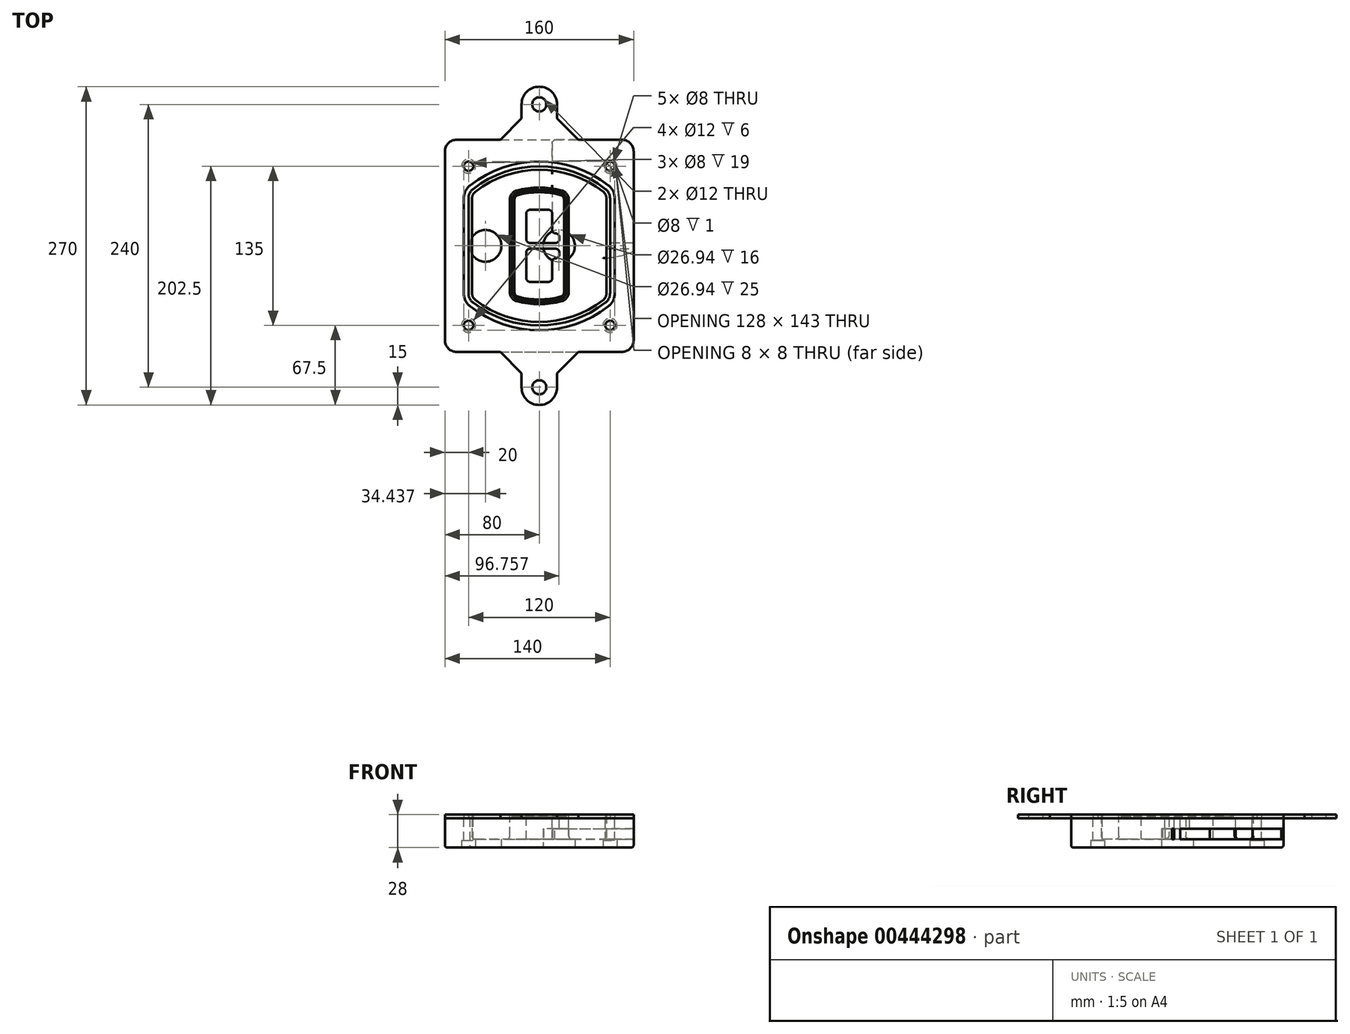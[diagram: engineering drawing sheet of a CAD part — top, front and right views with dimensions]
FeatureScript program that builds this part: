
annotation { "Feature Type Name" : "Feature", "Feature Type Description" : "" }
export const myFeature = defineFeature(function(context is Context, id is Id, definition is map)
    precondition{}
    {
        {
            var Q0;
            Q0=qCreatedBy(makeId("Top.planeOp"),FACE);
            var sketch = newSketch(context, id + "F0", { "sketchPlane" : qUnion([Q0])});
            skPoint(sketch, "E0.rect.middle", {"position": v(0, 0) * mm});
            skLineSegment(sketch, "E1.bottom", {"start": v(-70, -90) * mm, "end": v(70, -90) * mm});
            skLineSegment(sketch, "E1.top", {"start": v(-70, 90) * mm, "end": v(70, 90) * mm});
            skLineSegment(sketch, "E1.left", {"start": v(-80, -80) * mm, "end": v(-80, 80) * mm});
            skLineSegment(sketch, "E1.right", {"start": v(80, -80) * mm, "end": v(80, 80) * mm});
            skLineSegment(sketch, "E2", {"start": v(-80, 90) * mm, "end": v(80, -90) * mm, "construction": true});
            skLineSegment(sketch, "E3", {"start": v(80, 90) * mm, "end": v(-80, -90) * mm, "construction": true});
            skCircle(sketch, "E4", {"center": v(-60, 67.5) * mm, "radius": 4 * mm});
            skCircle(sketch, "E5", {"center": v(60, 67.5) * mm, "radius": 4 * mm});
            skCircle(sketch, "E6", {"center": v(60, -67.5) * mm, "radius": 4 * mm});
            skCircle(sketch, "E7", {"center": v(-60, -67.5) * mm, "radius": 4 * mm});
            skLineSegment(sketch, "E8", {"start": v(-60, 67.5) * mm, "end": v(60, 67.5) * mm, "construction": true});
            skLineSegment(sketch, "E9", {"start": v(60, 67.5) * mm, "end": v(60, -67.5) * mm, "construction": true});
            skLineSegment(sketch, "E10", {"start": v(60, -67.5) * mm, "end": v(-60, -67.5) * mm, "construction": true});
            skLineSegment(sketch, "E11", {"start": v(-60, -67.5) * mm, "end": v(-60, 67.5) * mm, "construction": true});
            skLineSegment(sketch, "E12", {"start": v(-60, 40.3) * mm, "end": v(-60, -40.3) * mm});
            skLineSegment(sketch, "E13", {"start": v(60, 40.3) * mm, "end": v(60, -40.3) * mm});
            skArc(sketch, "E14", {"start": v(56.15, 48.18) * mm, "mid": v(0, 67.5) * mm, "end": v(-56.15, 48.18) * mm});
            skArc(sketch, "E15", {"start": v(-56.15, -48.18) * mm, "mid": v(0, -67.5) * mm, "end": v(56.15, -48.18) * mm});
            skLineSegment(sketch, "E16", {"start": v(-60, 0) * mm, "end": v(60, 0) * mm, "construction": true});
            skPoint(sketch, "E17.visualSharp", {"position": v(-60, -45) * mm});
            skArc(sketch, "E17.filletArc", {"start": v(-60, -40.3) * mm, "mid": v(-58.99, -44.68) * mm, "end": v(-56.15, -48.18) * mm});
            skPoint(sketch, "E18.visualSharp", {"position": v(-60, 45) * mm});
            skArc(sketch, "E18.filletArc", {"start": v(-56.15, 48.18) * mm, "mid": v(-58.99, 44.68) * mm, "end": v(-60, 40.3) * mm});
            skPoint(sketch, "E19.visualSharp", {"position": v(60, 45) * mm});
            skArc(sketch, "E19.filletArc", {"start": v(60, 40.3) * mm, "mid": v(58.99, 44.68) * mm, "end": v(56.15, 48.18) * mm});
            skPoint(sketch, "E20.visualSharp", {"position": v(60, -45) * mm});
            skArc(sketch, "E20.filletArc", {"start": v(56.15, -48.18) * mm, "mid": v(58.99, -44.68) * mm, "end": v(60, -40.3) * mm});
            skPoint(sketch, "E21.visualSharp", {"position": v(-80, 90) * mm});
            skArc(sketch, "E21.filletArc", {"start": v(-70, 90) * mm, "mid": v(-77.07, 87.07) * mm, "end": v(-80, 80) * mm});
            skPoint(sketch, "E22.visualSharp", {"position": v(80, 90) * mm});
            skArc(sketch, "E22.filletArc", {"start": v(80, 80) * mm, "mid": v(77.07, 87.07) * mm, "end": v(70, 90) * mm});
            skPoint(sketch, "E23.visualSharp", {"position": v(80, -90) * mm});
            skArc(sketch, "E23.filletArc", {"start": v(70, -90) * mm, "mid": v(77.07, -87.07) * mm, "end": v(80, -80) * mm});
            skPoint(sketch, "E24.visualSharp", {"position": v(-80, -90) * mm});
            skArc(sketch, "E24.filletArc", {"start": v(-80, -80) * mm, "mid": v(-77.07, -87.07) * mm, "end": v(-70, -90) * mm});
            skArc(sketch, "E25.0", {"start": v(57, 40.3) * mm, "mid": v(56.3, 43.36) * mm, "end": v(54.3, 45.81) * mm});
            skLineSegment(sketch, "E25.1", {"start": v(57, 40.3) * mm, "end": v(57, -40.3) * mm});
            skArc(sketch, "E25.2", {"start": v(54.3, -45.81) * mm, "mid": v(56.3, -43.36) * mm, "end": v(57, -40.3) * mm});
            skArc(sketch, "E25.3", {"start": v(-54.3, -45.81) * mm, "mid": v(0, -64.5) * mm, "end": v(54.3, -45.81) * mm});
            skArc(sketch, "E25.4", {"start": v(-57, -40.3) * mm, "mid": v(-56.3, -43.36) * mm, "end": v(-54.3, -45.81) * mm});
            skArc(sketch, "E25.5", {"start": v(54.3, 45.81) * mm, "mid": v(0, 64.5) * mm, "end": v(-54.3, 45.81) * mm});
            skLineSegment(sketch, "E25.6", {"start": v(-57, 40.3) * mm, "end": v(-57, -40.3) * mm});
            skArc(sketch, "E25.7", {"start": v(-54.3, 45.81) * mm, "mid": v(-56.3, 43.36) * mm, "end": v(-57, 40.3) * mm});
            skArc(sketch, "E26.0", {"start": v(-58.62, 51.33) * mm, "mid": v(-62.58, 46.43) * mm, "end": v(-64, 40.3) * mm});
            skArc(sketch, "E26.1", {"start": v(58.62, 51.33) * mm, "mid": v(0, 71.5) * mm, "end": v(-58.62, 51.33) * mm});
            skArc(sketch, "E26.2", {"start": v(64, 40.3) * mm, "mid": v(62.58, 46.43) * mm, "end": v(58.62, 51.33) * mm});
            skLineSegment(sketch, "E26.3", {"start": v(64, 40.3) * mm, "end": v(64, -40.3) * mm});
            skArc(sketch, "E26.4", {"start": v(58.62, -51.33) * mm, "mid": v(62.58, -46.43) * mm, "end": v(64, -40.3) * mm});
            skLineSegment(sketch, "E26.5", {"start": v(-64, 40.3) * mm, "end": v(-64, -40.3) * mm});
            skArc(sketch, "E26.6", {"start": v(-58.62, -51.33) * mm, "mid": v(0, -71.5) * mm, "end": v(58.62, -51.33) * mm});
            skArc(sketch, "E26.7", {"start": v(-64, -40.3) * mm, "mid": v(-62.58, -46.43) * mm, "end": v(-58.62, -51.33) * mm});
            skCircle(sketch, "E27", {"center": v(0, 120) * mm, "radius": 6 * mm});
            skLineSegment(sketch, "E28", {"start": v(-15, 108) * mm, "end": v(-15, 120) * mm});
            skLineSegment(sketch, "E29", {"start": v(15, 108) * mm, "end": v(15, 120) * mm});
            skArc(sketch, "E30", {"start": v(15, 120) * mm, "mid": v(0, 135) * mm, "end": v(-15, 120) * mm});
            skLineSegment(sketch, "E31", {"start": v(-33, 90) * mm, "end": v(-15, 108) * mm});
            skLineSegment(sketch, "E32", {"start": v(15, 108) * mm, "end": v(33, 90) * mm});
            skLineSegment(sketch, "E33.MirrorCS", {"start": v(-33, -90) * mm, "end": v(-15, -108) * mm});
            skLineSegment(sketch, "E34.MirrorCS", {"start": v(-15, -108) * mm, "end": v(-15, -120) * mm});
            skCircle(sketch, "E35.MirrorC", {"center": v(0, -120) * mm, "radius": 6 * mm});
            skArc(sketch, "E36.MirrorCS", {"start": v(15, -120) * mm, "mid": v(0, -135) * mm, "end": v(-15, -120) * mm});
            skLineSegment(sketch, "E37.MirrorCS", {"start": v(15, -108) * mm, "end": v(15, -120) * mm});
            skLineSegment(sketch, "E38.MirrorCS", {"start": v(15, -108) * mm, "end": v(33, -90) * mm});
            skSolve(sketch);
        }
        {
            var Q0;
            Q0=makeQuery(id+"F0.imprint","IMPRINT",FACE,{"disambiguationData":[TD([[makeQuery(id+"F0.imprint","IMPRINT",EDGE,{"derivedFrom":sQuery(id+"F0.wireOp",EDGE,"E1.bottom")}),1.0]])]});
            var Q1;
            Q1=makeQuery(id+"F0.imprint","IMPRINT",FACE,{"disambiguationData":[TD([[makeQuery(id+"F0.imprint","IMPRINT",EDGE,{"derivedFrom":sQuery(id+"F0.wireOp",EDGE,"E12")}),1.0]])]});
            var Q2;
            Q2=makeQuery(id+"F0.imprint","IMPRINT",FACE,{"disambiguationData":[TD([[makeQuery(id+"F0.imprint","IMPRINT",EDGE,{"derivedFrom":sQuery(id+"F0.wireOp",EDGE,"E25.0")}),1.0]])]});
            var Q3;
            Q3=makeQuery(id+"F0.imprint","IMPRINT",FACE,{"disambiguationData":[TD([[makeQuery(id+"F0.imprint","IMPRINT",EDGE,{"derivedFrom":sQuery(id+"F0.wireOp",EDGE,"E12")}),-1.0]])]});
            extrude(context, id + "F1", {"entities" : qUnion([Q0, Q1, Q2, Q3]), "oppositeDirection" : true, "depth" : 25 * mm});
        }
        {
            var Q0;
            Q0=makeQuery(id+"F0.imprint","IMPRINT",FACE,{"disambiguationData":[TD([[makeQuery(id+"F0.imprint","IMPRINT",EDGE,{"derivedFrom":sQuery(id+"F0.wireOp",EDGE,"E12")}),1.0]])]});
            extrude(context, id + "F2", {"entities" : qUnion([Q0]), "operationType" : NewBodyOperationType.ADD, "depth" : 3 * mm});
        }
        {
            var Q0;
            Q0=makeQuery(id+"F0.imprint","IMPRINT",FACE,{"disambiguationData":[TD([[makeQuery(id+"F0.imprint","IMPRINT",EDGE,{"derivedFrom":sQuery(id+"F0.wireOp",EDGE,"E25.0")}),1.0]])]});
            extrude(context, id + "F3", {"entities" : qUnion([Q0]), "operationType" : NewBodyOperationType.REMOVE, "oppositeDirection" : true, "depth" : 18 * mm});
        }
        {
            var Q0;
            Q0=makeQuery(id+"F1.opExtrude","CAP_FACE",FACE,{"disambiguationData":[OSD([sQuery(id+"F0.wireOp",EDGE,"E1.bottom"),sQuery(id+"F0.wireOp",EDGE,"E1.top"),sQuery(id+"F0.wireOp",EDGE,"E1.left"),sQuery(id+"F0.wireOp",EDGE,"E1.right"),sQuery(id+"F0.wireOp",EDGE,"E4"),sQuery(id+"F0.wireOp",EDGE,"E5"),sQuery(id+"F0.wireOp",EDGE,"E6"),sQuery(id+"F0.wireOp",EDGE,"E7"),sQuery(id+"F0.wireOp",EDGE,"E21.filletArc"),sQuery(id+"F0.wireOp",EDGE,"E22.filletArc"),sQuery(id+"F0.wireOp",EDGE,"E23.filletArc"),sQuery(id+"F0.wireOp",EDGE,"E24.filletArc")])],"isStart":false});
            var sketch = newSketch(context, id + "F4", { "sketchPlane" : qUnion([Q0])});
            skCircle(sketch, "E39", {"center": v(16.76, 0) * mm, "radius": 13.47 * mm});
            skCircle(sketch, "E40", {"center": v(-45.56, 0) * mm, "radius": 13.47 * mm});
            skLineSegment(sketch, "E41", {"start": v(80, 0) * mm, "end": v(-80, 0) * mm});
            skCircle(sketch, "E42", {"center": v(16.76, 0) * mm, "radius": 18.47 * mm});
            skCircle(sketch, "E43", {"center": v(60, -67.5) * mm, "radius": 6 * mm});
            skCircle(sketch, "E44", {"center": v(-60, -67.5) * mm, "radius": 6 * mm});
            skCircle(sketch, "E45", {"center": v(-60, 67.5) * mm, "radius": 6 * mm});
            skCircle(sketch, "E46", {"center": v(60, 67.5) * mm, "radius": 6 * mm});
            skSolve(sketch);
        }
        {
            var Q0;
            Q0=makeQuery(id+"F2.opExtrude","CAP_FACE",FACE,{"disambiguationData":[OSD([sQuery(id+"F0.wireOp",EDGE,"E12"),sQuery(id+"F0.wireOp",EDGE,"E13"),sQuery(id+"F0.wireOp",EDGE,"E14"),sQuery(id+"F0.wireOp",EDGE,"E15"),sQuery(id+"F0.wireOp",EDGE,"E17.filletArc"),sQuery(id+"F0.wireOp",EDGE,"E18.filletArc"),sQuery(id+"F0.wireOp",EDGE,"E19.filletArc"),sQuery(id+"F0.wireOp",EDGE,"E20.filletArc"),sQuery(id+"F0.wireOp",EDGE,"E25.0"),sQuery(id+"F0.wireOp",EDGE,"E25.1"),sQuery(id+"F0.wireOp",EDGE,"E25.2"),sQuery(id+"F0.wireOp",EDGE,"E25.3"),sQuery(id+"F0.wireOp",EDGE,"E25.4"),sQuery(id+"F0.wireOp",EDGE,"E25.5"),sQuery(id+"F0.wireOp",EDGE,"E25.6"),sQuery(id+"F0.wireOp",EDGE,"E25.7")])],"isStart":false});
            var sketch = newSketch(context, id + "F5", { "sketchPlane" : qUnion([Q0])});
            skArc(sketch, "E47.0", {"start": v(-19.08, -46.97) * mm, "mid": v(0, -49.5) * mm, "end": v(19.08, -46.97) * mm});
            skArc(sketch, "E48.0", {"start": v(19.08, 46.97) * mm, "mid": v(0, 49.5) * mm, "end": v(-19.08, 46.97) * mm});
            skLineSegment(sketch, "E49", {"start": v(-25, 39.25) * mm, "end": v(-25, -39.25) * mm});
            skLineSegment(sketch, "E50", {"start": v(25, 39.25) * mm, "end": v(25, -39.25) * mm});
            skLineSegment(sketch, "E51", {"start": v(-25, 45.1) * mm, "end": v(25, 45.1) * mm, "construction": true});
            skLineSegment(sketch, "E52", {"start": v(-25, -45.1) * mm, "end": v(25, -45.1) * mm, "construction": true});
            skPoint(sketch, "E53.visualSharp", {"position": v(-25, 45.1) * mm});
            skArc(sketch, "E53.filletArc", {"start": v(-19.08, 46.97) * mm, "mid": v(-23.35, 44.11) * mm, "end": v(-25, 39.25) * mm});
            skPoint(sketch, "E54.visualSharp", {"position": v(25, 45.1) * mm});
            skArc(sketch, "E54.filletArc", {"start": v(25, 39.25) * mm, "mid": v(23.35, 44.11) * mm, "end": v(19.08, 46.97) * mm});
            skPoint(sketch, "E55.visualSharp", {"position": v(25, -45.1) * mm});
            skArc(sketch, "E55.filletArc", {"start": v(19.08, -46.97) * mm, "mid": v(23.35, -44.11) * mm, "end": v(25, -39.25) * mm});
            skPoint(sketch, "E56.visualSharp", {"position": v(-25, -45.1) * mm});
            skArc(sketch, "E56.filletArc", {"start": v(-25, -39.25) * mm, "mid": v(-23.35, -44.11) * mm, "end": v(-19.08, -46.97) * mm});
            skArc(sketch, "E57.0", {"start": v(54.3, 45.81) * mm, "mid": v(0, 64.5) * mm, "end": v(-54.3, 45.81) * mm});
            skArc(sketch, "E57.1", {"start": v(-54.3, 45.81) * mm, "mid": v(-56.3, 43.36) * mm, "end": v(-57, 40.3) * mm});
            skLineSegment(sketch, "E57.2", {"start": v(-57, 40.3) * mm, "end": v(-57, -40.3) * mm});
            skArc(sketch, "E57.3", {"start": v(-57, -40.3) * mm, "mid": v(-56.3, -43.36) * mm, "end": v(-54.3, -45.81) * mm});
            skArc(sketch, "E57.4", {"start": v(-54.3, -45.81) * mm, "mid": v(0, -64.5) * mm, "end": v(54.3, -45.81) * mm});
            skArc(sketch, "E57.5", {"start": v(54.3, -45.81) * mm, "mid": v(56.3, -43.36) * mm, "end": v(57, -40.3) * mm});
            skLineSegment(sketch, "E57.6", {"start": v(57, 40.3) * mm, "end": v(57, -40.3) * mm});
            skArc(sketch, "E57.7", {"start": v(57, 40.3) * mm, "mid": v(56.3, 43.36) * mm, "end": v(54.3, 45.81) * mm});
            skLineSegment(sketch, "E58.0", {"start": v(23, 39.25) * mm, "end": v(23, -39.25) * mm});
            skArc(sketch, "E58.1", {"start": v(18.56, -45.04) * mm, "mid": v(21.76, -42.9) * mm, "end": v(23, -39.25) * mm});
            skArc(sketch, "E58.2", {"start": v(-18.56, -45.04) * mm, "mid": v(0, -47.5) * mm, "end": v(18.56, -45.04) * mm});
            skArc(sketch, "E58.3", {"start": v(-23, -39.25) * mm, "mid": v(-21.76, -42.9) * mm, "end": v(-18.56, -45.04) * mm});
            skLineSegment(sketch, "E58.4", {"start": v(-23, 39.25) * mm, "end": v(-23, -39.25) * mm});
            skArc(sketch, "E58.5", {"start": v(23, 39.25) * mm, "mid": v(21.76, 42.9) * mm, "end": v(18.56, 45.04) * mm});
            skArc(sketch, "E58.6", {"start": v(-18.56, 45.04) * mm, "mid": v(-21.76, 42.9) * mm, "end": v(-23, 39.25) * mm});
            skArc(sketch, "E58.7", {"start": v(18.56, 45.04) * mm, "mid": v(0, 47.5) * mm, "end": v(-18.56, 45.04) * mm});
            skArc(sketch, "E59.0", {"start": v(21, 39.25) * mm, "mid": v(20.18, 41.68) * mm, "end": v(18.04, 43.1) * mm});
            skLineSegment(sketch, "E59.1", {"start": v(21, 39.25) * mm, "end": v(21, -39.25) * mm});
            skArc(sketch, "E59.2", {"start": v(18.04, -43.1) * mm, "mid": v(20.18, -41.68) * mm, "end": v(21, -39.25) * mm});
            skArc(sketch, "E59.3", {"start": v(-18.04, -43.1) * mm, "mid": v(0, -45.5) * mm, "end": v(18.04, -43.1) * mm});
            skArc(sketch, "E59.4", {"start": v(-21, -39.25) * mm, "mid": v(-20.18, -41.68) * mm, "end": v(-18.04, -43.1) * mm});
            skArc(sketch, "E59.5", {"start": v(18.04, 43.1) * mm, "mid": v(0, 45.5) * mm, "end": v(-18.04, 43.1) * mm});
            skLineSegment(sketch, "E59.6", {"start": v(-21, 39.25) * mm, "end": v(-21, -39.25) * mm});
            skArc(sketch, "E59.7", {"start": v(-18.04, 43.1) * mm, "mid": v(-20.18, 41.68) * mm, "end": v(-21, 39.25) * mm});
            skLineSegment(sketch, "E60", {"start": v(-25, 0) * mm, "end": v(25, 0) * mm, "construction": true});
            skLineSegment(sketch, "E61", {"start": v(-11, 5.5) * mm, "end": v(-11, 27.5) * mm});
            skLineSegment(sketch, "E62", {"start": v(-8, 30.5) * mm, "end": v(8, 30.5) * mm});
            skLineSegment(sketch, "E63", {"start": v(11, 27.5) * mm, "end": v(11, 13.5) * mm});
            skLineSegment(sketch, "E64", {"start": v(14, 10.5) * mm, "end": v(14, 10.5) * mm});
            skLineSegment(sketch, "E65", {"start": v(17, 7.5) * mm, "end": v(17, 5.5) * mm});
            skLineSegment(sketch, "E66", {"start": v(14, 2.5) * mm, "end": v(-8, 2.5) * mm});
            skPoint(sketch, "E67.visualSharp", {"position": v(-11, 30.5) * mm});
            skArc(sketch, "E67.filletArc", {"start": v(-8, 30.5) * mm, "mid": v(-10.12, 29.62) * mm, "end": v(-11, 27.5) * mm});
            skPoint(sketch, "E68.visualSharp", {"position": v(11, 30.5) * mm});
            skArc(sketch, "E68.filletArc", {"start": v(11, 27.5) * mm, "mid": v(10.12, 29.62) * mm, "end": v(8, 30.5) * mm});
            skPoint(sketch, "E69.visualSharp", {"position": v(11, 10.5) * mm});
            skArc(sketch, "E69.filletArc", {"start": v(11, 13.5) * mm, "mid": v(11.88, 11.38) * mm, "end": v(14, 10.5) * mm});
            skPoint(sketch, "E70.visualSharp", {"position": v(17, 10.5) * mm});
            skArc(sketch, "E70.filletArc", {"start": v(17, 7.5) * mm, "mid": v(16.12, 9.62) * mm, "end": v(14, 10.5) * mm});
            skPoint(sketch, "E71.visualSharp", {"position": v(17, 2.5) * mm});
            skArc(sketch, "E71.filletArc", {"start": v(14, 2.5) * mm, "mid": v(16.12, 3.38) * mm, "end": v(17, 5.5) * mm});
            skPoint(sketch, "E72.visualSharp", {"position": v(-11, 2.5) * mm});
            skArc(sketch, "E72.filletArc", {"start": v(-11, 5.5) * mm, "mid": v(-10.12, 3.38) * mm, "end": v(-8, 2.5) * mm});
            skLineSegment(sketch, "E73.0.MirrorCS", {"start": v(14, -2.5) * mm, "end": v(-8, -2.5) * mm});
            skArc(sketch, "E74.0.MirrorCS", {"start": v(-11, -5.5) * mm, "mid": v(-10.12, -3.38) * mm, "end": v(-8, -2.5) * mm});
            skLineSegment(sketch, "E75.0.MirrorCS", {"start": v(-11, -5.5) * mm, "end": v(-11, -27.5) * mm});
            skArc(sketch, "E76.0.MirrorCS", {"start": v(-8, -30.5) * mm, "mid": v(-10.12, -29.62) * mm, "end": v(-11, -27.5) * mm});
            skLineSegment(sketch, "E77.0.MirrorCS", {"start": v(-8, -30.5) * mm, "end": v(8, -30.5) * mm});
            skArc(sketch, "E78.0.MirrorCS", {"start": v(11, -27.5) * mm, "mid": v(10.12, -29.62) * mm, "end": v(8, -30.5) * mm});
            skLineSegment(sketch, "E79.0.MirrorCS", {"start": v(11, -27.5) * mm, "end": v(11, -13.5) * mm});
            skArc(sketch, "E80.0.MirrorCS", {"start": v(11, -13.5) * mm, "mid": v(11.88, -11.38) * mm, "end": v(14, -10.5) * mm});
            skArc(sketch, "E81.0.MirrorCS", {"start": v(17, -7.5) * mm, "mid": v(16.12, -9.62) * mm, "end": v(14, -10.5) * mm});
            skLineSegment(sketch, "E82.0.MirrorCS", {"start": v(17, -7.5) * mm, "end": v(17, -5.5) * mm});
            skArc(sketch, "E83.0.MirrorCS", {"start": v(14, -2.5) * mm, "mid": v(16.12, -3.38) * mm, "end": v(17, -5.5) * mm});
            skSolve(sketch);
        }
        {
            var Q0;
            Q0=makeQuery(id+"F5.imprint","IMPRINT",FACE,{"disambiguationData":[TD([[makeQuery(id+"F5.imprint","IMPRINT",EDGE,{"derivedFrom":sQuery(id+"F5.wireOp",EDGE,"E47.0")}),1.0]])]});
            var Q1;
            Q1=makeQuery(id+"F5.imprint","IMPRINT",FACE,{"disambiguationData":[TD([[makeQuery(id+"F5.imprint","IMPRINT",EDGE,{"derivedFrom":sQuery(id+"F5.wireOp",EDGE,"E58.0")}),-1.0]])]});
            var Q2;
            Q2=makeQuery(id+"F5.imprint","IMPRINT",FACE,{"disambiguationData":[TD([[makeQuery(id+"F5.imprint","IMPRINT",EDGE,{"derivedFrom":sQuery(id+"F5.wireOp",EDGE,"E59.0")}),1.0]])]});
            extrude(context, id + "F6", {"entities" : qUnion([Q0, Q1, Q2]), "operationType" : NewBodyOperationType.ADD, "endBound" : BoundingType.UP_TO_NEXT, "oppositeDirection" : true, "depth" : 25 * mm});
        }
        {
            var Q0;
            Q0=makeQuery(id+"F5.imprint","IMPRINT",FACE,{"disambiguationData":[TD([[makeQuery(id+"F5.imprint","IMPRINT",EDGE,{"derivedFrom":sQuery(id+"F5.wireOp",EDGE,"E58.0")}),-1.0]])]});
            extrude(context, id + "F7", {"entities" : qUnion([Q0]), "operationType" : NewBodyOperationType.REMOVE, "oppositeDirection" : true, "depth" : 2 * mm});
        }
        {
            var Q0;
            {var subQ0=sQuery(id+"F4.wireOp",EDGE,"E41");var subQ1=sQuery(id+"F4.wireOp",EDGE,"E39");var subQ3=makeQuery(id+"F4.imprint","INTERSECT",VERTEX,{"disambiguationData":[OD(0.0)],"derivedFrom":[subQ1,subQ0]});Q0=makeQuery(id+"F4.imprint","IMPRINT",FACE,{"disambiguationData":[TD([[makeQuery(id+"F4.imprint","IMPRINT",EDGE,{"disambiguationData":[TD([[subQ3,-1.0]])],"derivedFrom":subQ1}),1.0]])]});}
            var Q1;
            {var subQ0=sQuery(id+"F4.wireOp",EDGE,"E41");var subQ1=sQuery(id+"F4.wireOp",EDGE,"E39");var subQ3=makeQuery(id+"F4.imprint","INTERSECT",VERTEX,{"disambiguationData":[OD(0.0)],"derivedFrom":[subQ1,subQ0]});Q1=makeQuery(id+"F4.imprint","IMPRINT",FACE,{"disambiguationData":[TD([[makeQuery(id+"F4.imprint","IMPRINT",EDGE,{"disambiguationData":[TD([[subQ3,1.0]])],"derivedFrom":subQ1}),1.0]])]});}
            extrude(context, id + "F8", {"entities" : qUnion([Q0, Q1]), "operationType" : NewBodyOperationType.REMOVE, "oppositeDirection" : true, "depth" : 16 * mm});
        }
        {
            var Q0;
            {var subQ0=sQuery(id+"F4.wireOp",EDGE,"E41");var subQ1=sQuery(id+"F4.wireOp",EDGE,"E40");var subQ3=makeQuery(id+"F4.imprint","INTERSECT",VERTEX,{"disambiguationData":[OD(0.0)],"derivedFrom":[subQ1,subQ0]});Q0=makeQuery(id+"F4.imprint","IMPRINT",FACE,{"disambiguationData":[TD([[makeQuery(id+"F4.imprint","IMPRINT",EDGE,{"disambiguationData":[TD([[subQ3,-1.0]])],"derivedFrom":subQ1}),1.0]])]});}
            var Q1;
            {var subQ0=sQuery(id+"F4.wireOp",EDGE,"E41");var subQ1=sQuery(id+"F4.wireOp",EDGE,"E40");var subQ3=makeQuery(id+"F4.imprint","INTERSECT",VERTEX,{"disambiguationData":[OD(0.0)],"derivedFrom":[subQ1,subQ0]});Q1=makeQuery(id+"F4.imprint","IMPRINT",FACE,{"disambiguationData":[TD([[makeQuery(id+"F4.imprint","IMPRINT",EDGE,{"disambiguationData":[TD([[subQ3,1.0]])],"derivedFrom":subQ1}),1.0]])]});}
            extrude(context, id + "F9", {"entities" : qUnion([Q0, Q1]), "operationType" : NewBodyOperationType.REMOVE, "oppositeDirection" : true, "depth" : 25 * mm});
        }
        {
            var Q0;
            Q0=makeQuery(id+"F4.imprint","IMPRINT",FACE,{"disambiguationData":[TD([[makeQuery(id+"F4.imprint","IMPRINT",EDGE,{"derivedFrom":sQuery(id+"F4.wireOp",EDGE,"E43")}),1.0]])]});
            var Q1;
            Q1=makeQuery(id+"F4.imprint","IMPRINT",FACE,{"disambiguationData":[TD([[makeQuery(id+"F4.imprint","IMPRINT",EDGE,{"derivedFrom":makeQuery(id+"F1.opExtrude","CAP_EDGE",EDGE,{"disambiguationData":[OSD([sQuery(id+"F0.wireOp",EDGE,"E5")])],"isStart":false})}),-1.0]])]});
            var Q2;
            Q2=makeQuery(id+"F4.imprint","IMPRINT",FACE,{"disambiguationData":[TD([[makeQuery(id+"F4.imprint","IMPRINT",EDGE,{"derivedFrom":sQuery(id+"F4.wireOp",EDGE,"E44")}),1.0]])]});
            var Q3;
            Q3=makeQuery(id+"F4.imprint","IMPRINT",FACE,{"disambiguationData":[TD([[makeQuery(id+"F4.imprint","IMPRINT",EDGE,{"derivedFrom":makeQuery(id+"F1.opExtrude","CAP_EDGE",EDGE,{"disambiguationData":[OSD([sQuery(id+"F0.wireOp",EDGE,"E4")])],"isStart":false})}),-1.0]])]});
            var Q4;
            Q4=makeQuery(id+"F4.imprint","IMPRINT",FACE,{"disambiguationData":[TD([[makeQuery(id+"F4.imprint","IMPRINT",EDGE,{"derivedFrom":sQuery(id+"F4.wireOp",EDGE,"E45")}),1.0]])]});
            var Q5;
            Q5=makeQuery(id+"F4.imprint","IMPRINT",FACE,{"disambiguationData":[TD([[makeQuery(id+"F4.imprint","IMPRINT",EDGE,{"derivedFrom":makeQuery(id+"F1.opExtrude","CAP_EDGE",EDGE,{"disambiguationData":[OSD([sQuery(id+"F0.wireOp",EDGE,"E7")])],"isStart":false})}),-1.0]])]});
            var Q6;
            Q6=makeQuery(id+"F4.imprint","IMPRINT",FACE,{"disambiguationData":[TD([[makeQuery(id+"F4.imprint","IMPRINT",EDGE,{"derivedFrom":sQuery(id+"F4.wireOp",EDGE,"E46")}),1.0]])]});
            var Q7;
            Q7=makeQuery(id+"F4.imprint","IMPRINT",FACE,{"disambiguationData":[TD([[makeQuery(id+"F4.imprint","IMPRINT",EDGE,{"derivedFrom":makeQuery(id+"F1.opExtrude","CAP_EDGE",EDGE,{"disambiguationData":[OSD([sQuery(id+"F0.wireOp",EDGE,"E6")])],"isStart":false})}),-1.0]])]});
            extrude(context, id + "F10", {"entities" : qUnion([Q0, Q1, Q2, Q3, Q4, Q5, Q6, Q7]), "operationType" : NewBodyOperationType.REMOVE, "oppositeDirection" : true, "depth" : 6 * mm});
        }
        {
            var Q0;
            Q0=makeQuery(id+"F8.boolean.opBoolean","COPY",FACE,{"derivedFrom":makeQuery(id+"F8.opExtrude","CAP_FACE",FACE,{"disambiguationData":[OSD([sQuery(id+"F4.wireOp",EDGE,"E39")])],"isStart":false})});
            var sketch = newSketch(context, id + "F11", { "sketchPlane" : qUnion([Q0])});
            skArc(sketch, "E84.0", {"start": v(11, -88.19) * mm, "mid": v(97.1, -83.6) * mm, "end": v(92.5, 2.5) * mm});
            skArc(sketch, "E84.1", {"start": v(92.5, -2.5) * mm, "mid": v(-5.53, -19.03) * mm, "end": v(11, -117.08) * mm});
            skLineSegment(sketch, "E85", {"start": v(14, -2.5) * mm, "end": v(92.5, -2.5) * mm});
            skLineSegment(sketch, "E86.0", {"start": v(92.5, 2.5) * mm, "end": v(14, 2.5) * mm});
            skArc(sketch, "E86.1", {"start": v(14, 2.5) * mm, "mid": v(16.12, 3.38) * mm, "end": v(17, 5.5) * mm});
            skLineSegment(sketch, "E86.2", {"start": v(17, 7.5) * mm, "end": v(17, 5.5) * mm});
            skArc(sketch, "E86.3", {"start": v(17, 7.5) * mm, "mid": v(16.12, 9.62) * mm, "end": v(14, 10.5) * mm});
            skArc(sketch, "E86.4", {"start": v(11, 13.5) * mm, "mid": v(11.88, 11.38) * mm, "end": v(14, 10.5) * mm});
            skLineSegment(sketch, "E86.5", {"start": v(11, 13.5) * mm, "end": v(11, -88.19) * mm});
            skLineSegment(sketch, "E86.7", {"start": v(92.5, -2.5) * mm, "end": v(14, -2.5) * mm});
            skArc(sketch, "E86.8", {"start": v(14, -2.5) * mm, "mid": v(16.12, -3.38) * mm, "end": v(17, -5.5) * mm});
            skLineSegment(sketch, "E86.9", {"start": v(17, -7.5) * mm, "end": v(17, -5.5) * mm});
            skArc(sketch, "E86.10", {"start": v(17, -7.5) * mm, "mid": v(16.12, -9.62) * mm, "end": v(14, -10.5) * mm});
            skArc(sketch, "E86.11", {"start": v(11, -13.5) * mm, "mid": v(11.88, -11.38) * mm, "end": v(14, -10.5) * mm});
            skLineSegment(sketch, "E86.12", {"start": v(11, -117.08) * mm, "end": v(11, -13.5) * mm});
            skPoint(sketch, "E87.orphan", {"position": v(11, -27.5) * mm});
            skPoint(sketch, "E88.orphan", {"position": v(-8, -2.5) * mm});
            skPoint(sketch, "E89.orphan", {"position": v(-8, 2.5) * mm});
            skPoint(sketch, "E90.orphan", {"position": v(11, 27.5) * mm});
            skSolve(sketch);
        }
        {
            var Q0;
            {var subQ7=sQuery(id+"F11.wireOp",EDGE,"E84.0");var subQ14=sQuery(id+"F11.wireOp",EDGE,"E84.1");var subQ16=sQuery(id+"F11.wireOp",EDGE,"E86.1");var subQ18=sQuery(id+"F11.wireOp",EDGE,"E86.8");Q0=qUnion([makeQuery(id+"F11.imprint","IMPRINT",FACE,{"disambiguationData":[TD([[makeQuery(id+"F11.imprint","IMPRINT",EDGE,{"derivedFrom":subQ7}),1.0]])]}),makeQuery(id+"F11.imprint","IMPRINT",FACE,{"disambiguationData":[TD([[makeQuery(id+"F11.imprint","IMPRINT",EDGE,{"derivedFrom":subQ14}),1.0]])]}),makeQuery(id+"F11.imprint","IMPRINT",FACE,{"disambiguationData":[TD([[makeQuery(id+"F11.imprint","IMPRINT",EDGE,{"derivedFrom":subQ16}),1.0]])]}),makeQuery(id+"F11.imprint","IMPRINT",FACE,{"disambiguationData":[TD([[makeQuery(id+"F11.imprint","IMPRINT",EDGE,{"derivedFrom":subQ18}),-1.0]])]})]);}
            var Q1;
            Q1=makeQuery(id+"F6.boolean.opBoolean","SPLIT",FACE,{"disambiguationData":[TD([makeQuery(id+"F6.opExtrude","SWEPT_FACE",FACE,{"disambiguationData":[OSD([sQuery(id+"F5.wireOp",EDGE,"E61")])]})])],"derivedFrom":makeQuery(id+"F3.boolean.opBoolean","COPY",FACE,{"derivedFrom":makeQuery(id+"F3.opExtrude","CAP_FACE",FACE,{"disambiguationData":[OSD([sQuery(id+"F0.wireOp",EDGE,"E25.0"),sQuery(id+"F0.wireOp",EDGE,"E25.1"),sQuery(id+"F0.wireOp",EDGE,"E25.2"),sQuery(id+"F0.wireOp",EDGE,"E25.3"),sQuery(id+"F0.wireOp",EDGE,"E25.4"),sQuery(id+"F0.wireOp",EDGE,"E25.5"),sQuery(id+"F0.wireOp",EDGE,"E25.6"),sQuery(id+"F0.wireOp",EDGE,"E25.7")])],"isStart":false})})});
            extrude(context, id + "F12", {"entities" : qUnion([Q0]), "operationType" : NewBodyOperationType.REMOVE, "endBound" : BoundingType.UP_TO_SURFACE, "endBoundEntityFace" : qUnion([Q1]), "depth" : 25 * mm});
        }
        {
            var Q0;
            Q0=makeQuery(id+"F3.boolean.opBoolean","COPY",EDGE,{"derivedFrom":makeQuery(id+"F3.opExtrude","CAP_EDGE",EDGE,{"disambiguationData":[OSD([sQuery(id+"F0.wireOp",EDGE,"E25.6")])],"isStart":false})});
            var Q1;
            Q1=makeQuery(id+"FcX3RilgP8JfTuH_1.boolean.opBoolean","INTERSECT",EDGE,{"derivedFrom":[makeQuery(id+"F6.opExtrude","SWEPT_FACE",FACE,{"disambiguationData":[OSD([sQuery(id+"F5.wireOp",EDGE,"E50")])]}),makeQuery(id+"FcX3RilgP8JfTuH_1.opExtrude","CAP_FACE",FACE,{"disambiguationData":[OSD([sQuery(id+"F4.wireOp",EDGE,"E42")])],"isStart":false})]});
            var Q2;
            Q2=makeQuery(id+"FcX3RilgP8JfTuH_1.boolean.opBoolean","INTERSECT",EDGE,{"disambiguationData":[OD(1.0)],"derivedFrom":[makeQuery(id+"F6.opExtrude","SWEPT_FACE",FACE,{"disambiguationData":[OSD([sQuery(id+"F5.wireOp",EDGE,"E50")])]}),makeQuery(id+"FcX3RilgP8JfTuH_1.opExtrude","SWEPT_FACE",FACE,{"disambiguationData":[OSD([sQuery(id+"F4.wireOp",EDGE,"E42")])]})]});
            var Q3;
            {var subQ0=sQuery(id+"F5.wireOp",EDGE,"E50");Q3=makeQuery(id+"F8.boolean.opBoolean","SPLIT",EDGE,{"disambiguationData":[TD([makeQuery(id+"F6.opExtrude","SWEPT_FACE",FACE,{"disambiguationData":[OSD([sQuery(id+"F5.wireOp",EDGE,"E55.filletArc")])]})])],"derivedFrom":makeQuery(id+"F6.opExtrude","CAP_EDGE",EDGE,{"disambiguationData":[OSD([subQ0])],"isStart":false})});}
            var Q4;
            {var subQ0=sQuery(id+"F0.wireOp",EDGE,"E25.0");var subQ1=sQuery(id+"F0.wireOp",EDGE,"E25.1");var subQ2=sQuery(id+"F0.wireOp",EDGE,"E25.2");var subQ3=sQuery(id+"F0.wireOp",EDGE,"E25.3");var subQ4=sQuery(id+"F0.wireOp",EDGE,"E25.4");var subQ5=sQuery(id+"F0.wireOp",EDGE,"E25.5");var subQ6=sQuery(id+"F0.wireOp",EDGE,"E25.6");var subQ7=sQuery(id+"F0.wireOp",EDGE,"E25.7");Q4=makeQuery(id+"FcX3RilgP8JfTuH_1.boolean.opBoolean","INTERSECT",EDGE,{"derivedFrom":[makeQuery(id+"F6.boolean.opBoolean","SPLIT",FACE,{"disambiguationData":[TD([makeQuery(id+"F2.opExtrude","SWEPT_FACE",FACE,{"disambiguationData":[OSD([subQ0])]})])],"derivedFrom":makeQuery(id+"F3.boolean.opBoolean","COPY",FACE,{"derivedFrom":makeQuery(id+"F3.opExtrude","CAP_FACE",FACE,{"disambiguationData":[OSD([subQ0,subQ1,subQ2,subQ3,subQ4,subQ5,subQ6,subQ7])],"isStart":false})})}),makeQuery(id+"FcX3RilgP8JfTuH_1.opExtrude","SWEPT_FACE",FACE,{"disambiguationData":[OSD([sQuery(id+"F4.wireOp",EDGE,"E42")])]})]});}
            var Q5;
            Q5=makeQuery(id+"FcX3RilgP8JfTuH_1.boolean.opBoolean","INTERSECT",EDGE,{"disambiguationData":[OD(0.0)],"derivedFrom":[makeQuery(id+"F6.opExtrude","SWEPT_FACE",FACE,{"disambiguationData":[OSD([sQuery(id+"F5.wireOp",EDGE,"E50")])]}),makeQuery(id+"FcX3RilgP8JfTuH_1.opExtrude","SWEPT_FACE",FACE,{"disambiguationData":[OSD([sQuery(id+"F4.wireOp",EDGE,"E42")])]})]});
            fillet(context, id + "F13", {"entities" : qUnion([Q0, Q1, Q2, Q3, Q4, Q5]), "radius" : 3 * mm, "tangentPropagation" : true, "allowEdgeOverflow" : false});
        }
        {
            var Q0;
            Q0=makeQuery(id+"F1.opExtrude","CAP_EDGE",EDGE,{"disambiguationData":[OSD([sQuery(id+"F0.wireOp",EDGE,"E1.bottom")])],"isStart":false});
            fillet(context, id + "F14", {"entities" : qUnion([Q0]), "radius" : 2 * mm, "tangentPropagation" : true, "allowEdgeOverflow" : false});
        }
        {
            var Q0;
            Q0 = qSketchRegion(id + "F0", true);
            var Q1;
            Q1=makeQuery(id+"F2.opExtrude","CAP_FACE",FACE,{"disambiguationData":[OSD([sQuery(id+"F0.wireOp",EDGE,"E12"),sQuery(id+"F0.wireOp",EDGE,"E13"),sQuery(id+"F0.wireOp",EDGE,"E14"),sQuery(id+"F0.wireOp",EDGE,"E15"),sQuery(id+"F0.wireOp",EDGE,"E17.filletArc"),sQuery(id+"F0.wireOp",EDGE,"E18.filletArc"),sQuery(id+"F0.wireOp",EDGE,"E19.filletArc"),sQuery(id+"F0.wireOp",EDGE,"E20.filletArc"),sQuery(id+"F0.wireOp",EDGE,"E25.0"),sQuery(id+"F0.wireOp",EDGE,"E25.1"),sQuery(id+"F0.wireOp",EDGE,"E25.2"),sQuery(id+"F0.wireOp",EDGE,"E25.3"),sQuery(id+"F0.wireOp",EDGE,"E25.4"),sQuery(id+"F0.wireOp",EDGE,"E25.5"),sQuery(id+"F0.wireOp",EDGE,"E25.6"),sQuery(id+"F0.wireOp",EDGE,"E25.7")])],"isStart":false});
            extrude(context, id + "F15", {"entities" : qUnion([Q0]), "endBound" : BoundingType.UP_TO_SURFACE, "endBoundEntityFace" : qUnion([Q1]), "depth" : 3.5 * mm});
        }
        {
            var Q0;
            Q0=makeQuery(id+"F15.opExtrude","SWEPT_BODY",BODY,{"disambiguationData":[OSD([sQuery(id+"F0.wireOp",EDGE,"E1.bottom"),sQuery(id+"F0.wireOp",EDGE,"E1.top"),sQuery(id+"F0.wireOp",EDGE,"E1.left"),sQuery(id+"F0.wireOp",EDGE,"E1.right"),sQuery(id+"F0.wireOp",EDGE,"E4"),sQuery(id+"F0.wireOp",EDGE,"E5"),sQuery(id+"F0.wireOp",EDGE,"E6"),sQuery(id+"F0.wireOp",EDGE,"E7"),sQuery(id+"F0.wireOp",EDGE,"E21.filletArc"),sQuery(id+"F0.wireOp",EDGE,"E22.filletArc"),sQuery(id+"F0.wireOp",EDGE,"E23.filletArc"),sQuery(id+"F0.wireOp",EDGE,"E24.filletArc"),sQuery(id+"F0.wireOp",EDGE,"E26.0"),sQuery(id+"F0.wireOp",EDGE,"E26.1"),sQuery(id+"F0.wireOp",EDGE,"E26.2"),sQuery(id+"F0.wireOp",EDGE,"E26.3"),sQuery(id+"F0.wireOp",EDGE,"E26.4"),sQuery(id+"F0.wireOp",EDGE,"E26.5"),sQuery(id+"F0.wireOp",EDGE,"E26.6"),sQuery(id+"F0.wireOp",EDGE,"E26.7"),sQuery(id+"F0.wireOp",EDGE,"E27"),sQuery(id+"F0.wireOp",EDGE,"E28"),sQuery(id+"F0.wireOp",EDGE,"E29"),sQuery(id+"F0.wireOp",EDGE,"E30"),sQuery(id+"F0.wireOp",EDGE,"E31"),sQuery(id+"F0.wireOp",EDGE,"E32"),sQuery(id+"F0.wireOp",EDGE,"E33.MirrorCS"),sQuery(id+"F0.wireOp",EDGE,"E34.MirrorCS"),sQuery(id+"F0.wireOp",EDGE,"E35.MirrorC"),sQuery(id+"F0.wireOp",EDGE,"E36.MirrorCS"),sQuery(id+"F0.wireOp",EDGE,"E37.MirrorCS"),sQuery(id+"F0.wireOp",EDGE,"E38.MirrorCS")])]});
            deleteBodies(context, id + "F16", {"entities" : qUnion([Q0])});
        }
        {
            var Q0;
            Q0 = qSketchRegion(id + "F0", true);
            var Q1;
            Q1=makeQuery(id+"F2.opExtrude","CAP_FACE",FACE,{"disambiguationData":[OSD([sQuery(id+"F0.wireOp",EDGE,"E12"),sQuery(id+"F0.wireOp",EDGE,"E13"),sQuery(id+"F0.wireOp",EDGE,"E14"),sQuery(id+"F0.wireOp",EDGE,"E15"),sQuery(id+"F0.wireOp",EDGE,"E17.filletArc"),sQuery(id+"F0.wireOp",EDGE,"E18.filletArc"),sQuery(id+"F0.wireOp",EDGE,"E19.filletArc"),sQuery(id+"F0.wireOp",EDGE,"E20.filletArc"),sQuery(id+"F0.wireOp",EDGE,"E25.0"),sQuery(id+"F0.wireOp",EDGE,"E25.1"),sQuery(id+"F0.wireOp",EDGE,"E25.2"),sQuery(id+"F0.wireOp",EDGE,"E25.3"),sQuery(id+"F0.wireOp",EDGE,"E25.4"),sQuery(id+"F0.wireOp",EDGE,"E25.5"),sQuery(id+"F0.wireOp",EDGE,"E25.6"),sQuery(id+"F0.wireOp",EDGE,"E25.7")])],"isStart":false});
            extrude(context, id + "F17", {"entities" : qUnion([Q0]), "endBound" : BoundingType.UP_TO_SURFACE, "endBoundEntityFace" : qUnion([Q1]), "depth" : 25 * mm});
        }
    });
